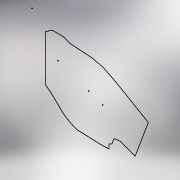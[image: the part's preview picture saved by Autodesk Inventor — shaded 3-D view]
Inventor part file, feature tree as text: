
AUTODESK INVENTOR PART (.ipt)
format: ipt  version: 2022 (Build 260153000, 153)  size: 111,104 bytes
history: native  units: mm
features: reference x8, other x3, sketch x2
ambient origin geometry x8: Origin, YZ Plane, XZ Plane, XY Plane, X Axis, Y Axis, Z Axis, Center Point
feature tree (13):
  sketch  "Sketch1"
  sketch  "Sketch2"
  reference  "Reference25"
  reference  "Reference26"
  reference  "Reference27"
  reference  "Reference28"
  reference  "Reference29"
  reference  "Reference30"
  reference  "Reference31"
  reference  "Reference32"
  other  "<userpath>\Desktop\fun\Chappy.iam"
  other  "Chappy.iam"
  other  "NEW:1"
